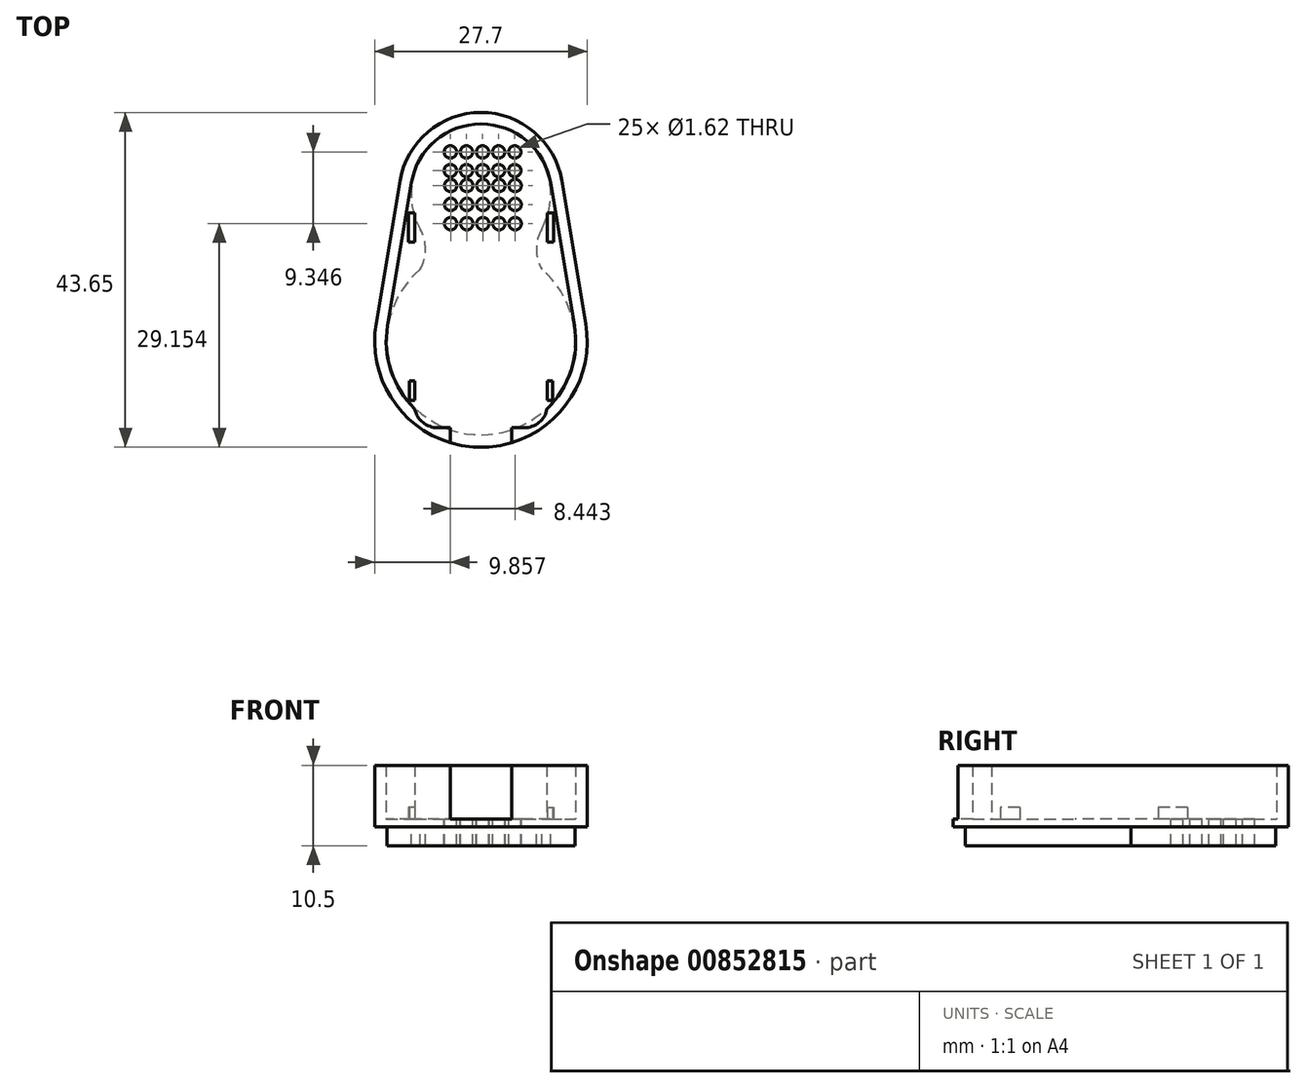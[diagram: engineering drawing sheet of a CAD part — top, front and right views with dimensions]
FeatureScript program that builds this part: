
annotation { "Feature Type Name" : "Feature", "Feature Type Description" : "" }
export const myFeature = defineFeature(function(context is Context, id is Id, definition is map)
    precondition{}
    {
        {
            var Q0;
            Q0=qCreatedBy(makeId("Top.planeOp"),FACE);
            var sketch = newSketch(context, id + "F0", { "sketchPlane" : qUnion([Q0])});
            skLineSegment(sketch, "E0", {"start": v(-8.01, 3.97) * mm, "end": v(8.01, 3.97) * mm});
            skArc(sketch, "E1", {"start": v(-8.01, 3.97) * mm, "mid": v(-10.75, 0.66) * mm, "end": v(-12.18, -3.4) * mm, "construction": true});
            skLineSegment(sketch, "E2", {"start": v(8.01, 3.97) * mm, "end": v(8.01, 3.97) * mm});
            skLineSegment(sketch, "E3", {"start": v(8.01, 9.14) * mm, "end": v(8.01, 9.14) * mm});
            skArc(sketch, "E4", {"start": v(-8.01, 3.97) * mm, "mid": v(-7.33, 6.56) * mm, "end": v(-8.01, 9.14) * mm, "construction": true});
            skLineSegment(sketch, "E5", {"start": v(-8.01, 9.14) * mm, "end": v(-8.01, 9.14) * mm});
            skArc(sketch, "E6", {"start": v(8.01, 9.14) * mm, "mid": v(7.33, 6.56) * mm, "end": v(8.01, 3.97) * mm, "construction": true});
            skArc(sketch, "E7", {"start": v(8.01, 9.14) * mm, "mid": v(8.01, 9.14) * mm, "end": v(8.01, 9.14) * mm});
            skArc(sketch, "E8", {"start": v(8.01, 9.14) * mm, "mid": v(9.06, 12.07) * mm, "end": v(9.07, 15.19) * mm, "construction": true});
            skArc(sketch, "E9", {"start": v(-8.01, 9.14) * mm, "mid": v(0, 4.47) * mm, "end": v(8.01, 9.14) * mm});
            skArc(sketch, "E10", {"start": v(-9.07, 15.19) * mm, "mid": v(-9.06, 12.07) * mm, "end": v(-8.01, 9.14) * mm, "construction": true});
            skLineSegment(sketch, "E11", {"start": v(-9.07, 15.19) * mm, "end": v(-9.07, 15.19) * mm});
            skArc(sketch, "E12", {"start": v(9.07, 15.19) * mm, "mid": v(0, 22.87) * mm, "end": v(-9.07, 15.19) * mm, "construction": true});
            skArc(sketch, "E13", {"start": v(12.18, -3.4) * mm, "mid": v(10.75, 0.66) * mm, "end": v(8.01, 3.97) * mm, "construction": true});
            skArc(sketch, "E14", {"start": v(-12.18, -3.4) * mm, "mid": v(0, -17.78) * mm, "end": v(12.18, -3.4) * mm, "construction": true});
            skLineSegment(sketch, "E15.0", {"start": v(-10.55, 15.43) * mm, "end": v(-13.66, -3.15) * mm});
            skArc(sketch, "E15.1", {"start": v(10.55, 15.43) * mm, "mid": v(0, 24.37) * mm, "end": v(-10.55, 15.43) * mm});
            skLineSegment(sketch, "E15.2", {"start": v(10.55, 15.43) * mm, "end": v(13.66, -3.15) * mm});
            skArc(sketch, "E15.3", {"start": v(-13.66, -3.15) * mm, "mid": v(0, -19.28) * mm, "end": v(13.66, -3.15) * mm});
            skPoint(sketch, "E16", {"position": v(12.35, -5.43) * mm});
            skPoint(sketch, "E17", {"position": v(-12.35, -5.43) * mm});
            skPoint(sketch, "E18", {"position": v(9, -5.43) * mm});
            skPoint(sketch, "E19", {"position": v(-9, -5.43) * mm});
            skLineSegment(sketch, "E20", {"start": v(0, -5.43) * mm, "end": v(0, -4.02) * mm});
            skLineSegment(sketch, "E21", {"start": v(0, -4.02) * mm, "end": v(0, -6.49) * mm});
            skArc(sketch, "E22.0", {"start": v(-7.93, 3.9) * mm, "mid": v(-10.65, 0.61) * mm, "end": v(-12.08, -3.41) * mm});
            skArc(sketch, "E22.1", {"start": v(-12.08, -3.41) * mm, "mid": v(0, -17.68) * mm, "end": v(12.08, -3.41) * mm});
            skArc(sketch, "E22.2", {"start": v(-7.93, 3.9) * mm, "mid": v(-7.23, 6.55) * mm, "end": v(-7.92, 9.2) * mm});
            skArc(sketch, "E22.3", {"start": v(12.08, -3.41) * mm, "mid": v(10.65, 0.61) * mm, "end": v(7.93, 3.9) * mm});
            skArc(sketch, "E22.4", {"start": v(-8.98, 15.17) * mm, "mid": v(-8.96, 12.1) * mm, "end": v(-7.92, 9.2) * mm});
            skArc(sketch, "E22.5", {"start": v(8.98, 15.17) * mm, "mid": v(0, 22.77) * mm, "end": v(-8.98, 15.17) * mm});
            skArc(sketch, "E22.6", {"start": v(7.92, 9.2) * mm, "mid": v(8.96, 12.1) * mm, "end": v(8.98, 15.17) * mm});
            skArc(sketch, "E22.7", {"start": v(7.92, 9.2) * mm, "mid": v(7.23, 6.55) * mm, "end": v(7.93, 3.9) * mm});
            skSolve(sketch);
        }
        {
            var Q0;
            Q0=makeQuery(id+"F0.imprint","IMPRINT",FACE,{"disambiguationData":[TD([[makeQuery(id+"F0.imprint","IMPRINT",EDGE,{"derivedFrom":sQuery(id+"F0.wireOp",EDGE,"E1")}),-1.0]])]});
            var Q1;
            Q1=makeQuery(id+"F0.imprint","IMPRINT",FACE,{"disambiguationData":[TD([[makeQuery(id+"F0.imprint","IMPRINT",EDGE,{"derivedFrom":sQuery(id+"F0.wireOp",EDGE,"E0")}),-1.0]])]});
            var Q2;
            Q2=makeQuery(id+"F0.imprint","IMPRINT",FACE,{"disambiguationData":[TD([[makeQuery(id+"F0.imprint","IMPRINT",EDGE,{"derivedFrom":sQuery(id+"F0.wireOp",EDGE,"E0")}),1.0]])]});
            var Q3;
            Q3=makeQuery(id+"F0.imprint","IMPRINT",FACE,{"disambiguationData":[TD([[makeQuery(id+"F0.imprint","IMPRINT",EDGE,{"derivedFrom":sQuery(id+"F0.wireOp",EDGE,"E7")}),1.0]])]});
            var Q4;
            {var subQ0=sQuery(id+"F0.wireOp",EDGE,"E22.0");Q4=makeQuery(id+"F0.imprint","IMPRINT",FACE,{"disambiguationData":[TD([[makeQuery(id+"F0.imprint","IMPRINT",EDGE,{"derivedFrom":subQ0}),1.0]])]});}
            var Q5;
            {var subQ0=sQuery(id+"F0.wireOp",EDGE,"E22.4");Q5=makeQuery(id+"F0.imprint","IMPRINT",FACE,{"disambiguationData":[TD([[makeQuery(id+"F0.imprint","IMPRINT",EDGE,{"derivedFrom":subQ0}),1.0]])]});}
            var Q6;
            Q6=makeQuery(id+"F0.imprint","IMPRINT",FACE,{"disambiguationData":[TD([[makeQuery(id+"F0.imprint","IMPRINT",EDGE,{"derivedFrom":sQuery(id+"F0.wireOp",EDGE,"E15.0")}),1.0]])]});
            extrude(context, id + "F1", {"entities" : qUnion([Q0, Q1, Q2, Q3, Q4, Q5, Q6]), "oppositeDirection" : true, "depth" : 1 * mm, "offsetDistance" : 25 * mm});
        }
        {
            var Q0;
            Q0=makeQuery(id+"F0.imprint","IMPRINT",FACE,{"disambiguationData":[TD([[makeQuery(id+"F0.imprint","IMPRINT",EDGE,{"derivedFrom":sQuery(id+"F0.wireOp",EDGE,"E7")}),1.0]])]});
            var Q1;
            Q1=makeQuery(id+"F0.imprint","IMPRINT",FACE,{"disambiguationData":[TD([[makeQuery(id+"F0.imprint","IMPRINT",EDGE,{"derivedFrom":sQuery(id+"F0.wireOp",EDGE,"E0")}),1.0]])]});
            var Q2;
            Q2=makeQuery(id+"F0.imprint","IMPRINT",FACE,{"disambiguationData":[TD([[makeQuery(id+"F0.imprint","IMPRINT",EDGE,{"derivedFrom":sQuery(id+"F0.wireOp",EDGE,"E0")}),-1.0]])]});
            var Q3;
            {var subQ0=sQuery(id+"F0.wireOp",EDGE,"E22.4");Q3=makeQuery(id+"F0.imprint","IMPRINT",FACE,{"disambiguationData":[TD([[makeQuery(id+"F0.imprint","IMPRINT",EDGE,{"derivedFrom":subQ0}),1.0]])]});}
            extrude(context, id + "F2", {"entities" : qUnion([Q0, Q1, Q2, Q3]), "operationType" : NewBodyOperationType.ADD, "oppositeDirection" : true, "depth" : 3.5 * mm, "offsetDistance" : 25 * mm});
        }
        {
            var Q0;
            Q0=makeQuery(id+"F1.opExtrude","CAP_FACE",FACE,{"disambiguationData":[OSD([sQuery(id+"F0.wireOp",EDGE,"E15.0"),sQuery(id+"F0.wireOp",EDGE,"E15.1"),sQuery(id+"F0.wireOp",EDGE,"E15.2"),sQuery(id+"F0.wireOp",EDGE,"E15.3")])],"isStart":true});
            var sketch = newSketch(context, id + "F3", { "sketchPlane" : qUnion([Q0])});
            skLineSegment(sketch, "E23.bottom", {"start": v(-8.65, 11.24) * mm, "end": v(8.65, 11.24) * mm, "construction": true});
            skLineSegment(sketch, "E23.top", {"start": v(-5.65, -16.76) * mm, "end": v(5.65, -16.76) * mm});
            skLineSegment(sketch, "E23.left", {"start": v(-8.65, 11.24) * mm, "end": v(-8.65, -13.76) * mm});
            skLineSegment(sketch, "E23.right", {"start": v(8.65, 11.24) * mm, "end": v(8.65, -13.76) * mm});
            skPoint(sketch, "E24", {"position": v(0, -16.76) * mm});
            skLineSegment(sketch, "E25.bottom", {"start": v(-4, -16.76) * mm, "end": v(4, -16.76) * mm});
            skLineSegment(sketch, "E25.top", {"start": v(-4, -17.96) * mm, "end": v(4, -17.96) * mm});
            skLineSegment(sketch, "E25.left", {"start": v(-4, -16.76) * mm, "end": v(-4, -17.96) * mm});
            skLineSegment(sketch, "E25.right", {"start": v(4, -16.76) * mm, "end": v(4, -17.96) * mm});
            skPoint(sketch, "E26", {"position": v(0, 11.24) * mm});
            skLineSegment(sketch, "E27", {"start": v(-4, -17.96) * mm, "end": v(-4, -19.56) * mm, "construction": true});
            skLineSegment(sketch, "E28", {"start": v(-4, -19.56) * mm, "end": v(4, -19.56) * mm, "construction": true});
            skLineSegment(sketch, "E29", {"start": v(4, -19.56) * mm, "end": v(4, -17.96) * mm, "construction": true});
            skPoint(sketch, "E30.visualSharp", {"position": v(-8.65, -16.76) * mm});
            skArc(sketch, "E30.filletArc", {"start": v(-8.65, -13.76) * mm, "mid": v(-7.77, -15.88) * mm, "end": v(-5.65, -16.76) * mm});
            skPoint(sketch, "E31.visualSharp", {"position": v(8.65, -16.76) * mm});
            skArc(sketch, "E31.filletArc", {"start": v(5.65, -16.76) * mm, "mid": v(7.77, -15.88) * mm, "end": v(8.65, -13.76) * mm});
            skLineSegment(sketch, "E32.0", {"start": v(-9.07, 15.19) * mm, "end": v(-12.18, -3.4) * mm});
            skArc(sketch, "E32.1", {"start": v(9.07, 15.19) * mm, "mid": v(0, 22.87) * mm, "end": v(-9.07, 15.19) * mm});
            skLineSegment(sketch, "E32.2", {"start": v(9.07, 15.19) * mm, "end": v(12.18, -3.4) * mm});
            skArc(sketch, "E32.3", {"start": v(-12.18, -3.4) * mm, "mid": v(-11.73, -9.28) * mm, "end": v(-8.6, -14.3) * mm});
            skArc(sketch, "E33", {"start": v(8.6, -14.3) * mm, "mid": v(11.73, -9.28) * mm, "end": v(12.18, -3.4) * mm});
            skLineSegment(sketch, "E34", {"start": v(4, -17.96) * mm, "end": v(4, -19.56) * mm});
            skLineSegment(sketch, "E35", {"start": v(-4, -19.56) * mm, "end": v(-4, -17.96) * mm});
            skLineSegment(sketch, "E36", {"start": v(4, -19.56) * mm, "end": v(-4, -19.56) * mm});
            skLineSegment(sketch, "E37.bottom", {"start": v(-8.65, 11.24) * mm, "end": v(-9.48, 11.24) * mm});
            skLineSegment(sketch, "E37.top", {"start": v(-8.65, 7.46) * mm, "end": v(-9.48, 7.46) * mm});
            skLineSegment(sketch, "E37.left", {"start": v(-8.65, 11.24) * mm, "end": v(-8.65, 7.46) * mm});
            skLineSegment(sketch, "E37.right", {"start": v(-9.48, 11.24) * mm, "end": v(-9.48, 7.46) * mm});
            skPoint(sketch, "E38.oppositeSnap0", {"position": v(-9.07, 7.46) * mm});
            skLineSegment(sketch, "E38.bottom", {"start": v(8.65, 11.24) * mm, "end": v(9.43, 11.24) * mm});
            skLineSegment(sketch, "E38.top", {"start": v(8.65, 7.46) * mm, "end": v(9.43, 7.46) * mm});
            skLineSegment(sketch, "E38.left", {"start": v(8.65, 11.24) * mm, "end": v(8.65, 7.46) * mm});
            skLineSegment(sketch, "E38.right", {"start": v(9.43, 11.24) * mm, "end": v(9.43, 7.46) * mm});
            skLineSegment(sketch, "E39.bottom", {"start": v(-8.65, -13.16) * mm, "end": v(-9.3, -13.16) * mm});
            skLineSegment(sketch, "E39.top", {"start": v(-8.65, -10.62) * mm, "end": v(-9.3, -10.62) * mm});
            skLineSegment(sketch, "E39.left", {"start": v(-8.65, -13.16) * mm, "end": v(-8.65, -10.62) * mm});
            skLineSegment(sketch, "E39.right", {"start": v(-9.3, -13.16) * mm, "end": v(-9.3, -10.62) * mm});
            skLineSegment(sketch, "E40.bottom", {"start": v(8.65, -13.16) * mm, "end": v(9.35, -13.16) * mm});
            skLineSegment(sketch, "E40.top", {"start": v(8.65, -10.62) * mm, "end": v(9.35, -10.62) * mm});
            skLineSegment(sketch, "E40.left", {"start": v(8.65, -13.16) * mm, "end": v(8.65, -10.62) * mm});
            skLineSegment(sketch, "E40.right", {"start": v(9.35, -13.16) * mm, "end": v(9.35, -10.62) * mm});
            skCircle(sketch, "E41", {"center": v(-4, 19.22) * mm, "radius": 0.8 * mm});
            skCircle(sketch, "E42.1.0.0", {"center": v(-1.9, 19.22) * mm, "radius": 0.8 * mm});
            skCircle(sketch, "E42.2.0.0", {"center": v(0.2, 19.22) * mm, "radius": 0.8 * mm});
            skCircle(sketch, "E42.3.0.0", {"center": v(2.3, 19.22) * mm, "radius": 0.8 * mm});
            skCircle(sketch, "E42.4.0.0", {"center": v(4.4, 19.22) * mm, "radius": 0.8 * mm});
            skLineSegment(sketch, "E42.direction1", {"start": v(-4, 19.22) * mm, "end": v(-1.9, 19.22) * mm, "construction": true});
            skCircle(sketch, "E43", {"center": v(-4, 16.79) * mm, "radius": 0.8 * mm});
            skCircle(sketch, "E44.1.0.0", {"center": v(-1.9, 16.79) * mm, "radius": 0.8 * mm});
            skCircle(sketch, "E44.2.0.0", {"center": v(0.2, 16.79) * mm, "radius": 0.8 * mm});
            skCircle(sketch, "E44.3.0.0", {"center": v(2.3, 16.79) * mm, "radius": 0.8 * mm});
            skCircle(sketch, "E44.4.0.0", {"center": v(4.4, 16.79) * mm, "radius": 0.8 * mm});
            skCircle(sketch, "E45", {"center": v(-3.95, 14.85) * mm, "radius": 0.8 * mm});
            skCircle(sketch, "E46.1.0.0", {"center": v(-1.85, 14.85) * mm, "radius": 0.8 * mm});
            skCircle(sketch, "E46.2.0.0", {"center": v(0.25, 14.85) * mm, "radius": 0.8 * mm});
            skCircle(sketch, "E46.3.0.0", {"center": v(2.35, 14.85) * mm, "radius": 0.8 * mm});
            skCircle(sketch, "E46.4.0.0", {"center": v(4.45, 14.85) * mm, "radius": 0.8 * mm});
            skCircle(sketch, "E47", {"center": v(-3.95, 12.38) * mm, "radius": 0.8 * mm});
            skCircle(sketch, "E48.1.0.0", {"center": v(-1.85, 12.38) * mm, "radius": 0.8 * mm});
            skCircle(sketch, "E48.2.0.0", {"center": v(0.25, 12.38) * mm, "radius": 0.8 * mm});
            skCircle(sketch, "E48.3.0.0", {"center": v(2.35, 12.38) * mm, "radius": 0.8 * mm});
            skCircle(sketch, "E48.4.0.0", {"center": v(4.45, 12.38) * mm, "radius": 0.8 * mm});
            skCircle(sketch, "E49", {"center": v(-3.95, 9.87) * mm, "radius": 0.8 * mm});
            skCircle(sketch, "E50.1.0.0", {"center": v(-1.85, 9.87) * mm, "radius": 0.8 * mm});
            skCircle(sketch, "E50.2.0.0", {"center": v(0.25, 9.87) * mm, "radius": 0.8 * mm});
            skCircle(sketch, "E50.3.0.0", {"center": v(2.35, 9.87) * mm, "radius": 0.8 * mm});
            skCircle(sketch, "E50.4.0.0", {"center": v(4.45, 9.87) * mm, "radius": 0.8 * mm});
            skSolve(sketch);
        }
        {
            var Q0;
            {var subQ8=sQuery(id+"F3.wireOp",EDGE,"E25.left");Q0=makeQuery(id+"F3.imprint","IMPRINT",FACE,{"disambiguationData":[TD([[makeQuery(id+"F3.imprint","IMPRINT",EDGE,{"derivedFrom":subQ8}),-1.0]])]});}
            extrude(context, id + "F4", {"entities" : qUnion([Q0]), "operationType" : NewBodyOperationType.ADD, "depth" : 7 * mm, "offsetDistance" : 25 * mm});
        }
        {
            var Q0;
            Q0=makeQuery(id+"F3.imprint","IMPRINT",FACE,{"disambiguationData":[TD([[makeQuery(id+"F3.imprint","IMPRINT",EDGE,{"derivedFrom":sQuery(id+"F3.wireOp",EDGE,"E37.bottom")}),1.0]])]});
            var Q1;
            Q1=makeQuery(id+"F3.imprint","IMPRINT",FACE,{"disambiguationData":[TD([[makeQuery(id+"F3.imprint","IMPRINT",EDGE,{"derivedFrom":sQuery(id+"F3.wireOp",EDGE,"E38.bottom")}),-1.0]])]});
            var Q2;
            Q2=makeQuery(id+"F3.imprint","IMPRINT",FACE,{"disambiguationData":[TD([[makeQuery(id+"F3.imprint","IMPRINT",EDGE,{"derivedFrom":sQuery(id+"F3.wireOp",EDGE,"E40.bottom")}),1.0]])]});
            var Q3;
            Q3=makeQuery(id+"F3.imprint","IMPRINT",FACE,{"disambiguationData":[TD([[makeQuery(id+"F3.imprint","IMPRINT",EDGE,{"derivedFrom":sQuery(id+"F3.wireOp",EDGE,"E39.bottom")}),-1.0]])]});
            extrude(context, id + "F5", {"entities" : qUnion([Q0, Q1, Q2, Q3]), "operationType" : NewBodyOperationType.ADD, "depth" : 1.5 * mm, "offsetDistance" : 25 * mm});
        }
        {
            var Q0;
            Q0=makeQuery(id+"F3.imprint","IMPRINT",FACE,{"disambiguationData":[TD([[makeQuery(id+"F3.imprint","IMPRINT",EDGE,{"derivedFrom":sQuery(id+"F3.wireOp",EDGE,"E41")}),1.0]])]});
            var Q1;
            Q1=makeQuery(id+"F3.imprint","IMPRINT",FACE,{"disambiguationData":[TD([[makeQuery(id+"F3.imprint","IMPRINT",EDGE,{"derivedFrom":sQuery(id+"F3.wireOp",EDGE,"E42.1.0.0")}),1.0]])]});
            var Q2;
            Q2=makeQuery(id+"F3.imprint","IMPRINT",FACE,{"disambiguationData":[TD([[makeQuery(id+"F3.imprint","IMPRINT",EDGE,{"derivedFrom":sQuery(id+"F3.wireOp",EDGE,"E42.2.0.0")}),1.0]])]});
            var Q3;
            Q3=makeQuery(id+"F3.imprint","IMPRINT",FACE,{"disambiguationData":[TD([[makeQuery(id+"F3.imprint","IMPRINT",EDGE,{"derivedFrom":sQuery(id+"F3.wireOp",EDGE,"E42.3.0.0")}),1.0]])]});
            var Q4;
            Q4=makeQuery(id+"F3.imprint","IMPRINT",FACE,{"disambiguationData":[TD([[makeQuery(id+"F3.imprint","IMPRINT",EDGE,{"derivedFrom":sQuery(id+"F3.wireOp",EDGE,"E42.4.0.0")}),1.0]])]});
            var Q5;
            Q5=makeQuery(id+"F3.imprint","IMPRINT",FACE,{"disambiguationData":[TD([[makeQuery(id+"F3.imprint","IMPRINT",EDGE,{"derivedFrom":sQuery(id+"F3.wireOp",EDGE,"E44.4.0.0")}),1.0]])]});
            var Q6;
            Q6=makeQuery(id+"F3.imprint","IMPRINT",FACE,{"disambiguationData":[TD([[makeQuery(id+"F3.imprint","IMPRINT",EDGE,{"derivedFrom":sQuery(id+"F3.wireOp",EDGE,"E44.3.0.0")}),1.0]])]});
            var Q7;
            Q7=makeQuery(id+"F3.imprint","IMPRINT",FACE,{"disambiguationData":[TD([[makeQuery(id+"F3.imprint","IMPRINT",EDGE,{"derivedFrom":sQuery(id+"F3.wireOp",EDGE,"E44.2.0.0")}),1.0]])]});
            var Q8;
            Q8=makeQuery(id+"F3.imprint","IMPRINT",FACE,{"disambiguationData":[TD([[makeQuery(id+"F3.imprint","IMPRINT",EDGE,{"derivedFrom":sQuery(id+"F3.wireOp",EDGE,"E44.1.0.0")}),1.0]])]});
            var Q9;
            Q9=makeQuery(id+"F3.imprint","IMPRINT",FACE,{"disambiguationData":[TD([[makeQuery(id+"F3.imprint","IMPRINT",EDGE,{"derivedFrom":sQuery(id+"F3.wireOp",EDGE,"E43")}),1.0]])]});
            var Q10;
            Q10=makeQuery(id+"F3.imprint","IMPRINT",FACE,{"disambiguationData":[TD([[makeQuery(id+"F3.imprint","IMPRINT",EDGE,{"derivedFrom":sQuery(id+"F3.wireOp",EDGE,"E45")}),1.0]])]});
            var Q11;
            Q11=makeQuery(id+"F3.imprint","IMPRINT",FACE,{"disambiguationData":[TD([[makeQuery(id+"F3.imprint","IMPRINT",EDGE,{"derivedFrom":sQuery(id+"F3.wireOp",EDGE,"E46.1.0.0")}),1.0]])]});
            var Q12;
            Q12=makeQuery(id+"F3.imprint","IMPRINT",FACE,{"disambiguationData":[TD([[makeQuery(id+"F3.imprint","IMPRINT",EDGE,{"derivedFrom":sQuery(id+"F3.wireOp",EDGE,"E46.2.0.0")}),1.0]])]});
            var Q13;
            Q13=makeQuery(id+"F3.imprint","IMPRINT",FACE,{"disambiguationData":[TD([[makeQuery(id+"F3.imprint","IMPRINT",EDGE,{"derivedFrom":sQuery(id+"F3.wireOp",EDGE,"E46.3.0.0")}),1.0]])]});
            var Q14;
            Q14=makeQuery(id+"F3.imprint","IMPRINT",FACE,{"disambiguationData":[TD([[makeQuery(id+"F3.imprint","IMPRINT",EDGE,{"derivedFrom":sQuery(id+"F3.wireOp",EDGE,"E46.4.0.0")}),1.0]])]});
            var Q15;
            Q15=makeQuery(id+"F3.imprint","IMPRINT",FACE,{"disambiguationData":[TD([[makeQuery(id+"F3.imprint","IMPRINT",EDGE,{"derivedFrom":sQuery(id+"F3.wireOp",EDGE,"E47")}),1.0]])]});
            var Q16;
            Q16=makeQuery(id+"F3.imprint","IMPRINT",FACE,{"disambiguationData":[TD([[makeQuery(id+"F3.imprint","IMPRINT",EDGE,{"derivedFrom":sQuery(id+"F3.wireOp",EDGE,"E48.1.0.0")}),1.0]])]});
            var Q17;
            Q17=makeQuery(id+"F3.imprint","IMPRINT",FACE,{"disambiguationData":[TD([[makeQuery(id+"F3.imprint","IMPRINT",EDGE,{"derivedFrom":sQuery(id+"F3.wireOp",EDGE,"E48.2.0.0")}),1.0]])]});
            var Q18;
            Q18=makeQuery(id+"F3.imprint","IMPRINT",FACE,{"disambiguationData":[TD([[makeQuery(id+"F3.imprint","IMPRINT",EDGE,{"derivedFrom":sQuery(id+"F3.wireOp",EDGE,"E48.3.0.0")}),1.0]])]});
            var Q19;
            Q19=makeQuery(id+"F3.imprint","IMPRINT",FACE,{"disambiguationData":[TD([[makeQuery(id+"F3.imprint","IMPRINT",EDGE,{"derivedFrom":sQuery(id+"F3.wireOp",EDGE,"E48.4.0.0")}),1.0]])]});
            var Q20;
            Q20=makeQuery(id+"F3.imprint","IMPRINT",FACE,{"disambiguationData":[TD([[makeQuery(id+"F3.imprint","IMPRINT",EDGE,{"derivedFrom":sQuery(id+"F3.wireOp",EDGE,"E49")}),1.0]])]});
            var Q21;
            Q21=makeQuery(id+"F3.imprint","IMPRINT",FACE,{"disambiguationData":[TD([[makeQuery(id+"F3.imprint","IMPRINT",EDGE,{"derivedFrom":sQuery(id+"F3.wireOp",EDGE,"E50.1.0.0")}),1.0]])]});
            var Q22;
            Q22=makeQuery(id+"F3.imprint","IMPRINT",FACE,{"disambiguationData":[TD([[makeQuery(id+"F3.imprint","IMPRINT",EDGE,{"derivedFrom":sQuery(id+"F3.wireOp",EDGE,"E50.2.0.0")}),1.0]])]});
            var Q23;
            Q23=makeQuery(id+"F3.imprint","IMPRINT",FACE,{"disambiguationData":[TD([[makeQuery(id+"F3.imprint","IMPRINT",EDGE,{"derivedFrom":sQuery(id+"F3.wireOp",EDGE,"E50.3.0.0")}),1.0]])]});
            var Q24;
            Q24=makeQuery(id+"F3.imprint","IMPRINT",FACE,{"disambiguationData":[TD([[makeQuery(id+"F3.imprint","IMPRINT",EDGE,{"derivedFrom":sQuery(id+"F3.wireOp",EDGE,"E50.4.0.0")}),1.0]])]});
            extrude(context, id + "F6", {"entities" : qUnion([Q0, Q1, Q2, Q3, Q4, Q5, Q6, Q7, Q8, Q9, Q10, Q11, Q12, Q13, Q14, Q15, Q16, Q17, Q18, Q19, Q20, Q21, Q22, Q23, Q24]), "operationType" : NewBodyOperationType.REMOVE, "oppositeDirection" : true, "depth" : 5 * mm, "offsetDistance" : 25 * mm});
        }
    });
